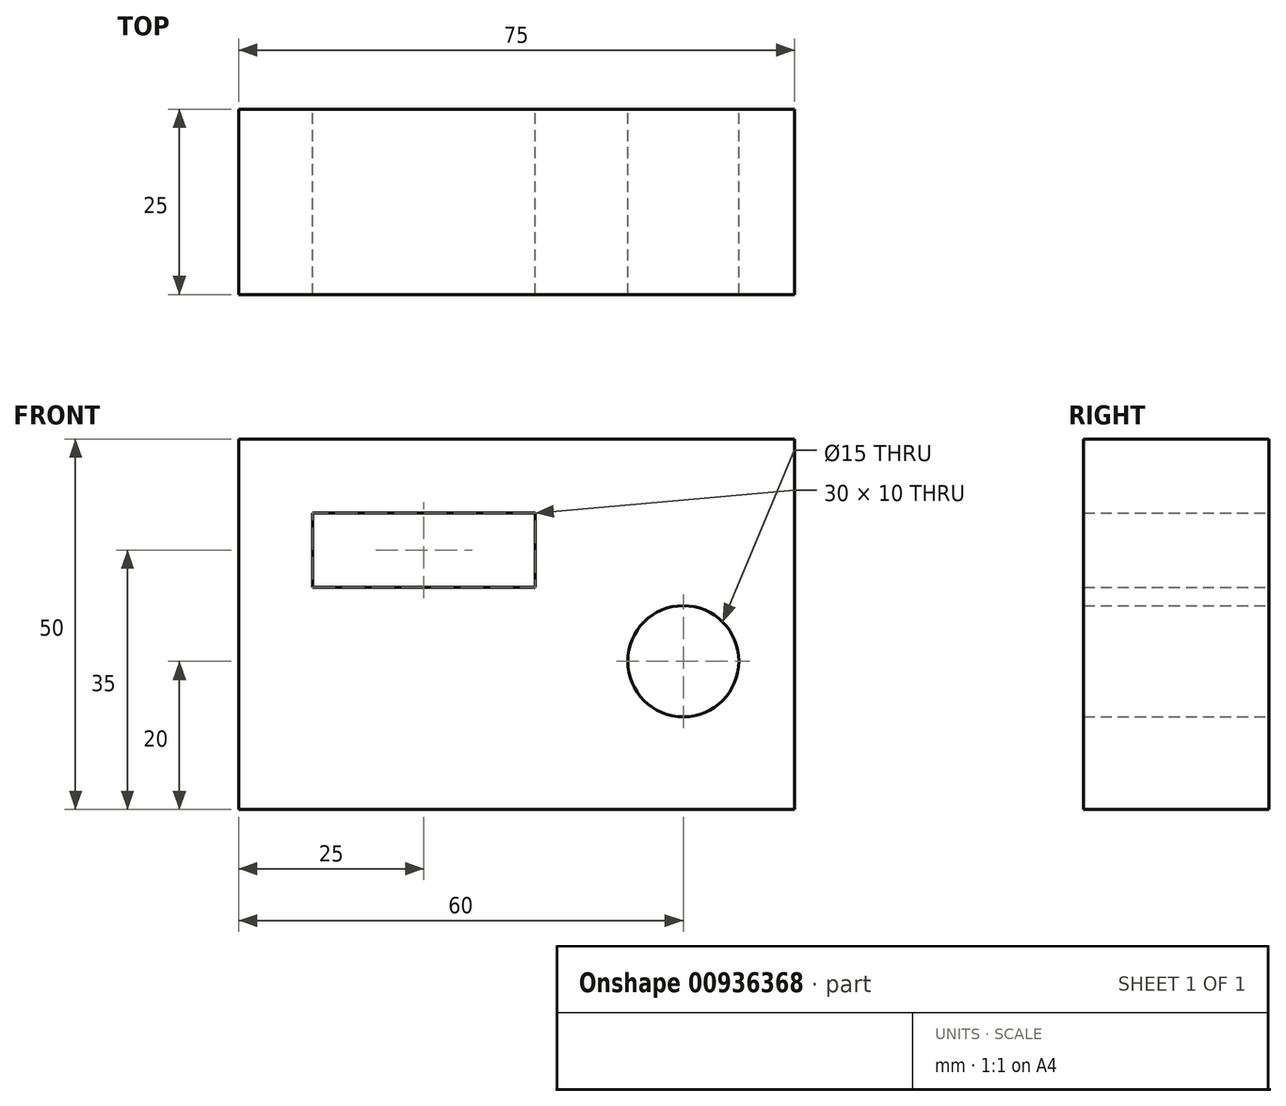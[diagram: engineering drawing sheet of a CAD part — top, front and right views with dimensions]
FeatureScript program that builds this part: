
annotation { "Feature Type Name" : "Feature", "Feature Type Description" : "" }
export const myFeature = defineFeature(function(context is Context, id is Id, definition is map)
    precondition{}
    {
        {
            var Q0;
            Q0=qCreatedBy(makeId("Front.planeOp"),FACE);
            var sketch = newSketch(context, id + "F0", { "sketchPlane" : qUnion([Q0])});
            skLineSegment(sketch, "E0", {"start": v(-60, -20) * mm, "end": v(15, -20) * mm});
            skLineSegment(sketch, "E1", {"start": v(15, -20) * mm, "end": v(15, 30) * mm});
            skLineSegment(sketch, "E2", {"start": v(15, 30) * mm, "end": v(-60, 30) * mm});
            skLineSegment(sketch, "E3", {"start": v(-60, 30) * mm, "end": v(-60, -20) * mm});
            skCircle(sketch, "E4", {"center": v(0, 0) * mm, "radius": 7.5 * mm});
            skLineSegment(sketch, "E5.bottom", {"start": v(-20, 10) * mm, "end": v(-50, 10) * mm});
            skLineSegment(sketch, "E5.top", {"start": v(-20, 20) * mm, "end": v(-50, 20) * mm});
            skLineSegment(sketch, "E5.left", {"start": v(-20, 10) * mm, "end": v(-20, 20) * mm});
            skLineSegment(sketch, "E5.right", {"start": v(-50, 10) * mm, "end": v(-50, 20) * mm});
            skPoint(sketch, "E5.middle", {"position": v(-35, 15) * mm});
            skSolve(sketch);
        }
        {
            var Q0;
            Q0 = qSketchRegion(id + "F0", true);
            extrude(context, id + "F1", {"entities" : qUnion([Q0]), "depth" : 25 * mm, "offsetDistance" : 25 * mm});
        }
    });
